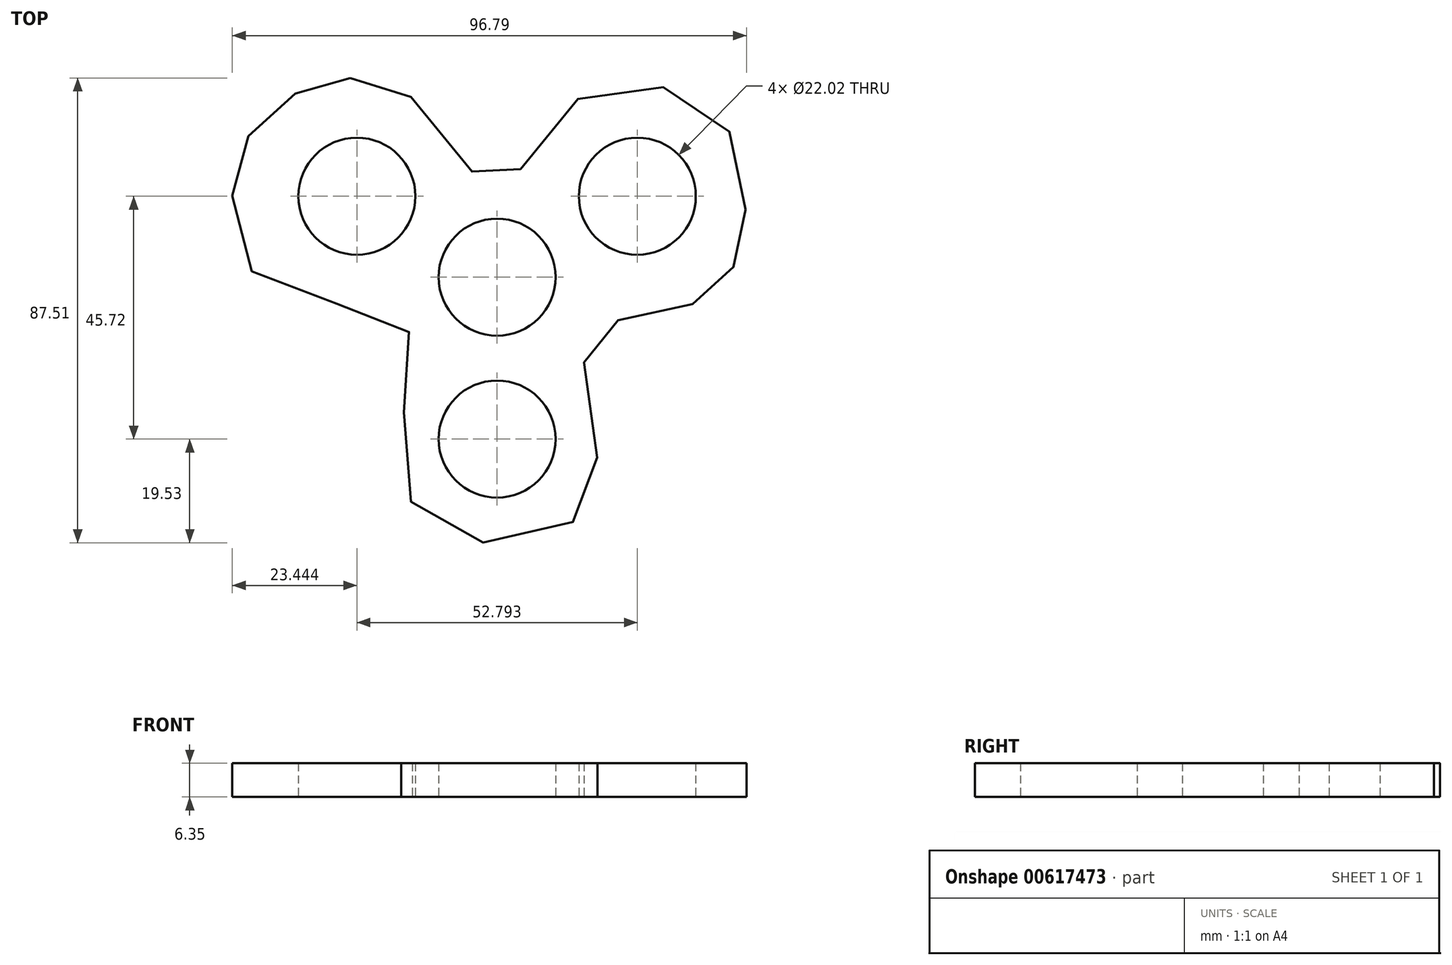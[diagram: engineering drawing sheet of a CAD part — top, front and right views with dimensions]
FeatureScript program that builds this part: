
annotation { "Feature Type Name" : "Feature", "Feature Type Description" : "" }
export const myFeature = defineFeature(function(context is Context, id is Id, definition is map)
    precondition{}
    {
        {
            var Q0;
            Q0=qCreatedBy(makeId("Top.planeOp"),FACE);
            var sketch = newSketch(context, id + "F0", { "sketchPlane" : qUnion([Q0])});
            skCircle(sketch, "E0", {"center": v(0, 0) * mm, "radius": 11.01 * mm});
            skLineSegment(sketch, "E1", {"start": v(0, 0) * mm, "end": v(26.4, 15.24) * mm});
            skLineSegment(sketch, "E2", {"start": v(0, 0) * mm, "end": v(0, -30.48) * mm});
            skLineSegment(sketch, "E3", {"start": v(0, 0) * mm, "end": v(-26.4, 15.24) * mm});
            skCircle(sketch, "E4", {"center": v(-26.4, 15.24) * mm, "radius": 11.01 * mm});
            skCircle(sketch, "E5", {"center": v(26.4, 15.24) * mm, "radius": 11.01 * mm});
            skCircle(sketch, "E6", {"center": v(0, -30.48) * mm, "radius": 11.01 * mm});
            skPoint(sketch, "E7.cCircle.perimeterSnap0", {"position": v(0, -15.24) * mm});
            skPoint(sketch, "E7.0.startSnap0", {"position": v(0, -15.24) * mm});
            skFitSpline(sketch, "E8", {"points": [v(-27.66, 37.46) * mm, v(-15.48, 33.25) * mm, v(0, 16.66) * mm, v(11.93, 31.04) * mm, v(33.64, 35.06) * mm, v(46.32, 21.51) * mm, v(45.34, 4.42) * mm, v(43.2, 0) * mm, v(30.94, -7.35) * mm, v(17.43, -10.25) * mm, v(18.82, -33.27) * mm, v(13.08, -46.85) * mm, v(-12.3, -47.04) * mm, v(-17.58, -25.84) * mm, v(-18.05, -8.27) * mm, v(-43.06, -1.67) * mm, v(-49.84, 15.27) * mm, v(-46.71, 26.7) * mm, v(-37.45, 34.85) * mm, v(-27.66, 37.46) * mm]});
            skSolve(sketch);
        }
        {
            var Q0;
            Q0 = qSketchRegion(id + "F0", true);
            extrude(context, id + "F1", {"entities" : qUnion([Q0]), "depth" : 6.35 * mm, "offsetDistance" : 25.4 * mm});
        }
    });
